# Revit family: ir_quattro_micro_053789
name_source: partatom
category: Leuchten
revit_build: Autodesk Revit 2016 (Build: 20190508_0715(x64)
units: mm (PartAtom-declared; Revit-internal decimal feet)

## family parameters
Basisbauteil = Fläche
Beim Laden mit Abzugskörper schneiden = Nein
Bemaßung runder Anschluss = Durchmesser verwenden
Gemeinsam genutzt = Nein
Lichtquelle = Nein
Raumberechnungspunkt = Nein
Teiletyp = Normal

## types (1)
- IR Quattro MICRO
    Beschreibung = Type: Presence detector; Dimensions (Ø x H): 43 x 70 mm; Mains power supply: 220 – 240 V / 50 – 60 Hz; Power consumption: 0,5 W; Sensor Technology: passive infrared; Application, place: Indoors; Application, room: one-person office, hotel room, care room, function room / ancillary room, WC / washroom, Indoors; Installation site: ceiling; Installation: Installation; Switching zones: 168 switching zones; Electronic scalability: No; Mechanical scalability: No; Mounting height: 2,00 – 5,00 m; Optimum mounting height: 2,8 m; Detection angle: 360 °; Angle of aperture: 90 °; Sneak-by guard: Yes; Capability of masking out individual segments: No; Reach, radial: 4 x 4 m (16 m²); Reach, tangential: 6 x 6 m (36 m²); Reach, presence: 4 x 4 m (16 m²); Twilight setting TEACH: Yes; Twilight setting: 2 – 1000 lx; Time setting: 5 sec – 60 min; Switching output 1, resistive: 1000 W; Switching output 1, number of LEDs / fluorescent lamps: 8 pcs.; Switching output 1, floating: No; Constant-lighting control: No; Basic light level function: No; Functions: Normal / test mode, Semi-/fully automatic, Manual ON / ON-OFF; Settings via: Remote control, Smart Remote; With remote control: No; Interconnection: Yes; IP-rating: IP65; Material: Plastic; Ambient temperature: -25 – 55 °C; Colour: white; Colour, RAL: 9003; Manufacturer's Warranty: 5 years; Version: COM1 - white; PU1, EAN: 4007841053789
    Frequency = 60 Hz, 50 Hz
    Height = 0 mm  [stored 0 ft]
    Hersteller = Steinel
    Lampe = 0 x
    Length = 200 mm
    Luminous efficacy = 0 lm/W
    ModVariant = Nein
    Modell = 053789
    Number of Poles = 1
    OnlyDefault = Ja
    Power Factor = 1
    Product Name = IR Quattro MICRO
    Product group = Sensor-switched indoor light
    ProductGroupID = 30
    Protection Class = Protection class
    Protection Degree = Degree of protection
    RlxData = <blob elided: 84757 chars, md5=12ac60ad>
    Scheinlast = 0 VA
    Standby Power = 0 W
    System Light Flux = 0 lm
    System Power = 0 W
    Typenbild = produkt1_053789.jpg
    Typenkommentare = Product without accessories
    URL = http://relux.com
    VarID = ---
    Voltage = 0 V
    Vorgabe-Ansicht = 1800 mm
    Weight = 0.00 kg
    Width = 100 mm  [stored 0.328084 ft]

note: [stored X ft] marks values corroborated as IEEE doubles in the binary element streams (Revit-internal decimal feet)

## geometry (parser evidence)
native form markers: Blend x4, Sweep x13
no freeform markers — native parametric forms only
